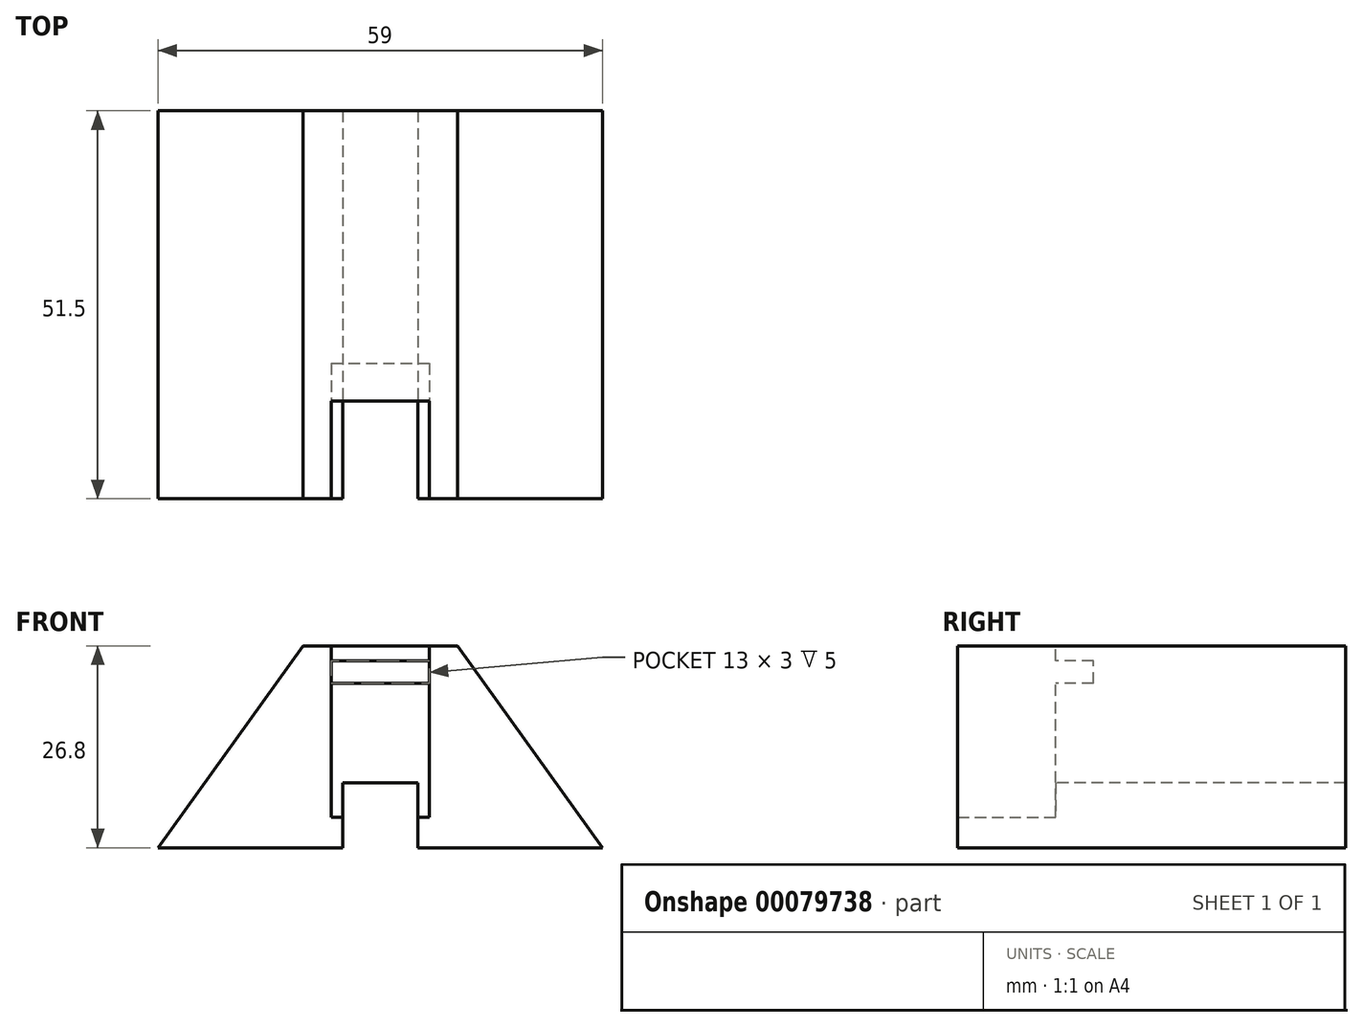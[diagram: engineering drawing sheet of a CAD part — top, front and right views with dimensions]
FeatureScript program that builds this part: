
annotation { "Feature Type Name" : "Feature", "Feature Type Description" : "" }
export const myFeature = defineFeature(function(context is Context, id is Id, definition is map)
    precondition{}
    {
        {
            var Q0;
            Q0=qCreatedBy(makeId("Top.planeOp"),FACE);
            var sketch = newSketch(context, id + "F0", { "sketchPlane" : qUnion([Q0])});
            skLineSegment(sketch, "E0.bottom", {"start": v(29.5, -25.75) * mm, "end": v(-29.5, -25.75) * mm});
            skLineSegment(sketch, "E0.top", {"start": v(29.5, 25.75) * mm, "end": v(-29.5, 25.75) * mm});
            skLineSegment(sketch, "E0.left", {"start": v(29.5, -25.75) * mm, "end": v(29.5, 25.75) * mm});
            skLineSegment(sketch, "E0.right", {"start": v(-29.5, -25.75) * mm, "end": v(-29.5, 25.75) * mm});
            skPoint(sketch, "E0.middle", {"position": v(0, 0) * mm});
            skSolve(sketch);
        }
        {
            var Q0;
            Q0 = qSketchRegion(id + "F0", true);
            extrude(context, id + "F1", {"entities" : qUnion([Q0]), "depth" : 26.8 * mm});
        }
        {
            var Q0;
            Q0=makeQuery(id+"F1.opExtrude","CAP_FACE",FACE,{"disambiguationData":[OSD([sQuery(id+"F0.wireOp",EDGE,"E0.bottom"),sQuery(id+"F0.wireOp",EDGE,"E0.top"),sQuery(id+"F0.wireOp",EDGE,"E0.left"),sQuery(id+"F0.wireOp",EDGE,"E0.right")])],"isStart":false});
            var sketch = newSketch(context, id + "F2", { "sketchPlane" : qUnion([Q0])});
            skLineSegment(sketch, "E1.bottom", {"start": v(-5, -12.75) * mm, "end": v(5, -12.75) * mm});
            skLineSegment(sketch, "E1.top", {"start": v(-5, -25.75) * mm, "end": v(5, -25.75) * mm});
            skLineSegment(sketch, "E1.left", {"start": v(-5, -12.75) * mm, "end": v(-5, -25.75) * mm});
            skLineSegment(sketch, "E1.right", {"start": v(5, -12.75) * mm, "end": v(5, -25.75) * mm});
            skPoint(sketch, "E1.middle", {"position": v(0, -19.25) * mm});
            skSolve(sketch);
        }
        {
            var Q0;
            Q0=makeQuery(id+"F2.imprint","IMPRINT",FACE,{"disambiguationData":[TD([[makeQuery(id+"F2.imprint","IMPRINT",EDGE,{"derivedFrom":sQuery(id+"F2.wireOp",EDGE,"E1.bottom")}),-1.0]])]});
            extrude(context, id + "F3", {"entities" : qUnion([Q0]), "operationType" : NewBodyOperationType.REMOVE, "oppositeDirection" : true, "depth" : 26.8 * mm});
        }
        {
            var Q0;
            Q0=makeQuery(id+"F1.opExtrude","CAP_FACE",FACE,{"disambiguationData":[OSD([sQuery(id+"F0.wireOp",EDGE,"E0.bottom"),sQuery(id+"F0.wireOp",EDGE,"E0.top"),sQuery(id+"F0.wireOp",EDGE,"E0.left"),sQuery(id+"F0.wireOp",EDGE,"E0.right")])],"isStart":false});
            var sketch = newSketch(context, id + "F4", { "sketchPlane" : qUnion([Q0])});
            skLineSegment(sketch, "E2.bottom", {"start": v(-6.5, -12.75) * mm, "end": v(6.5, -12.75) * mm});
            skLineSegment(sketch, "E2.top", {"start": v(-6.5, -25.75) * mm, "end": v(6.5, -25.75) * mm});
            skLineSegment(sketch, "E2.left", {"start": v(-6.5, -12.75) * mm, "end": v(-6.5, -25.75) * mm});
            skLineSegment(sketch, "E2.right", {"start": v(6.5, -12.75) * mm, "end": v(6.5, -25.75) * mm});
            skSolve(sketch);
        }
        {
            var Q0;
            Q0 = qSketchRegion(id + "F4", true);
            extrude(context, id + "F5", {"entities" : qUnion([Q0]), "operationType" : NewBodyOperationType.REMOVE, "oppositeDirection" : true, "depth" : 22.75 * mm});
        }
        {
            var Q0;
            {var subQ0=sQuery(id+"F0.wireOp",EDGE,"E0.right");var subQ3=sQuery(id+"F0.wireOp",EDGE,"E0.bottom");Q0=makeQuery(id+"F3.boolean.opBoolean","SPLIT",FACE,{"disambiguationData":[TD([makeQuery(id+"F1.opExtrude","SWEPT_FACE",FACE,{"disambiguationData":[OSD([subQ0])]})])],"derivedFrom":makeQuery(id+"F1.opExtrude","SWEPT_FACE",FACE,{"disambiguationData":[OSD([subQ3])]})});}
            var sketch = newSketch(context, id + "F6", { "sketchPlane" : qUnion([Q0])});
            skLineSegment(sketch, "E3", {"start": v(-29.5, 0) * mm, "end": v(-29.5, 26.8) * mm});
            skLineSegment(sketch, "E4", {"start": v(-29.5, 26.8) * mm, "end": v(-10.24, 26.8) * mm});
            skLineSegment(sketch, "E5", {"start": v(-10.24, 26.8) * mm, "end": v(-29.5, 0) * mm});
            skSolve(sketch);
        }
        {
            var Q0;
            Q0 = qSketchRegion(id + "F6", true);
            extrude(context, id + "F7", {"entities" : qUnion([Q0]), "operationType" : NewBodyOperationType.REMOVE, "oppositeDirection" : true, "depth" : 51.5 * mm});
        }
        {
            var Q0;
            {var subQ1=sQuery(id+"F0.wireOp",EDGE,"E0.left");var subQ3=sQuery(id+"F0.wireOp",EDGE,"E0.bottom");Q0=makeQuery(id+"F3.boolean.opBoolean","SPLIT",FACE,{"disambiguationData":[TD([makeQuery(id+"F1.opExtrude","SWEPT_FACE",FACE,{"disambiguationData":[OSD([subQ1])]})])],"derivedFrom":makeQuery(id+"F1.opExtrude","SWEPT_FACE",FACE,{"disambiguationData":[OSD([subQ3])]})});}
            var sketch = newSketch(context, id + "F8", { "sketchPlane" : qUnion([Q0])});
            skLineSegment(sketch, "E6", {"start": v(29.5, 0) * mm, "end": v(29.5, 26.8) * mm});
            skLineSegment(sketch, "E7", {"start": v(29.5, 26.8) * mm, "end": v(10.24, 26.8) * mm});
            skLineSegment(sketch, "E8", {"start": v(10.24, 26.8) * mm, "end": v(29.5, 0) * mm});
            skSolve(sketch);
        }
        {
            var Q0;
            Q0 = qSketchRegion(id + "F8", true);
            extrude(context, id + "F9", {"entities" : qUnion([Q0]), "operationType" : NewBodyOperationType.REMOVE, "oppositeDirection" : true, "depth" : 51.5 * mm});
        }
        {
            var Q0;
            Q0=makeQuery(id+"F5.boolean.opBoolean","MERGE",FACE,{"derivedFrom":[makeQuery(id+"F3.boolean.opBoolean","COPY",FACE,{"derivedFrom":makeQuery(id+"F3.opExtrude","SWEPT_FACE",FACE,{"disambiguationData":[OSD([sQuery(id+"F2.wireOp",EDGE,"E1.bottom")])]})}),makeQuery(id+"F5.opExtrude","SWEPT_FACE",FACE,{"disambiguationData":[OSD([sQuery(id+"F4.wireOp",EDGE,"E2.bottom")])]})]});
            var sketch = newSketch(context, id + "F10", { "sketchPlane" : qUnion([Q0])});
            skLineSegment(sketch, "E9.bottom", {"start": v(-5, 8.64) * mm, "end": v(5, 8.64) * mm});
            skLineSegment(sketch, "E9.top", {"start": v(-5, -0.03) * mm, "end": v(5, -0.03) * mm});
            skLineSegment(sketch, "E9.left", {"start": v(-5, 8.64) * mm, "end": v(-5, -0.03) * mm});
            skLineSegment(sketch, "E9.right", {"start": v(5, 8.64) * mm, "end": v(5, -0.03) * mm});
            skSolve(sketch);
        }
        {
            var Q0;
            Q0 = qSketchRegion(id + "F10", true);
            extrude(context, id + "F11", {"entities" : qUnion([Q0]), "operationType" : NewBodyOperationType.REMOVE, "oppositeDirection" : true, "depth" : 38.5 * mm});
        }
        {
            var Q0;
            Q0=makeQuery(id+"F5.boolean.opBoolean","MERGE",FACE,{"derivedFrom":[makeQuery(id+"F3.boolean.opBoolean","COPY",FACE,{"derivedFrom":makeQuery(id+"F3.opExtrude","SWEPT_FACE",FACE,{"disambiguationData":[OSD([sQuery(id+"F2.wireOp",EDGE,"E1.bottom")])]})}),makeQuery(id+"F5.opExtrude","SWEPT_FACE",FACE,{"disambiguationData":[OSD([sQuery(id+"F4.wireOp",EDGE,"E2.bottom")])]})]});
            var sketch = newSketch(context, id + "F12", { "sketchPlane" : qUnion([Q0])});
            skLineSegment(sketch, "E10.bottom", {"start": v(-6.5, 24.8) * mm, "end": v(6.5, 24.8) * mm});
            skLineSegment(sketch, "E10.top", {"start": v(-6.5, 21.8) * mm, "end": v(6.5, 21.8) * mm});
            skLineSegment(sketch, "E10.left", {"start": v(-6.5, 24.8) * mm, "end": v(-6.5, 21.8) * mm});
            skLineSegment(sketch, "E10.right", {"start": v(6.5, 24.8) * mm, "end": v(6.5, 21.8) * mm});
            skSolve(sketch);
        }
        {
            var Q0;
            Q0 = qSketchRegion(id + "F12", true);
            extrude(context, id + "F13", {"entities" : qUnion([Q0]), "operationType" : NewBodyOperationType.REMOVE, "oppositeDirection" : true, "depth" : 5 * mm});
        }
    });
